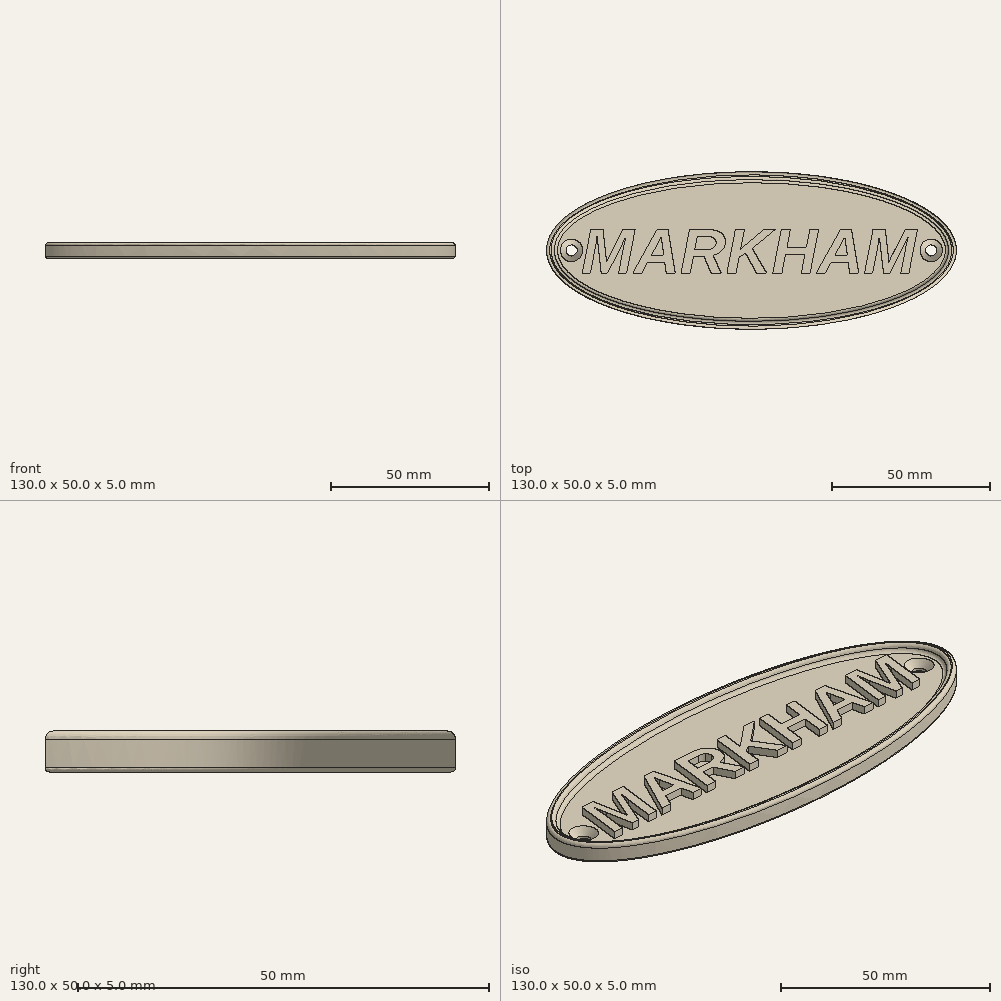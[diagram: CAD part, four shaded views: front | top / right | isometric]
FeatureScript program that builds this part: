
annotation { "Feature Type Name" : "Feature", "Feature Type Description" : "" }
export const myFeature = defineFeature(function(context is Context, id is Id, definition is map)
    precondition{}
    {
        {
            var Q0;
            Q0=qCreatedBy(makeId("Top.planeOp"),FACE);
            var sketch = newSketch(context, id + "F0", { "sketchPlane" : qUnion([Q0])});
            skEllipse(sketch, "E0", {"center": v(0, 0) * mm, "majorRadius": 65 * mm, "minorRadius": 25 * mm, "majorAxis": v(1, 0)});
            skSolve(sketch);
        }
        {
            var Q0;
            Q0=makeQuery(id+"F0.imprint","IMPRINT",FACE,{"disambiguationData":[TD([[makeQuery(id+"F0.imprint","IMPRINT",EDGE,{"derivedFrom":sQuery(id+"F0.wireOp",EDGE,"E0")}),1.0]])]});
            extrude(context, id + "F1", {"entities" : qUnion([Q0]), "depth" : 3 * mm, "offsetDistance" : 25 * mm});
        }
        {
            var Q0;
            Q0=makeQuery(id+"F1.opExtrude","CAP_FACE",FACE,{"disambiguationData":[OSD([sQuery(id+"F0.wireOp",EDGE,"E0")])],"isStart":false});
            var sketch = newSketch(context, id + "F2", { "sketchPlane" : qUnion([Q0])});
            skEllipse(sketch, "E1", {"center": v(0, 0) * mm, "majorRadius": 65 * mm, "minorRadius": 25 * mm, "majorAxis": v(1, 0)});
            skEllipse(sketch, "E2", {"center": v(0, 0) * mm, "majorRadius": 62.5 * mm, "minorRadius": 22.5 * mm, "majorAxis": v(1, 0)});
            skText(sketch, "E3", { "text": "MARKHAM", "fontName": "Arimo-BoldItalic.ttf"});
            const initialGuessF2  = {"E3": [-0.054, -0.00725, 1, 0, 0.0145]};
            skSetInitialGuess(sketch, initialGuessF2);
            skSolve(sketch);
        }
        {
            var Q0;
            Q0=makeQuery(id+"F2.imprint","IMPRINT",FACE,{"disambiguationData":[TD([[makeQuery(id+"F2.imprint","IMPRINT",EDGE,{"derivedFrom":sQuery(id+"F2.wireOp",EDGE,"E1")}),1.0]])]});
            var Q1;
            Q1=makeQuery(id+"F2.imprint","IMPRINT",FACE,{"disambiguationData":[TD([[makeQuery(id+"F2.imprint","IMPRINT",EDGE,{"derivedFrom":sQuery(id+"F2.wireOp",EDGE,"E3.sketch_text.stroke-0")}),-1.0]])]});
            var Q2;
            Q2=makeQuery(id+"F2.imprint","IMPRINT",FACE,{"disambiguationData":[TD([[makeQuery(id+"F2.imprint","IMPRINT",EDGE,{"derivedFrom":sQuery(id+"F2.wireOp",EDGE,"E3.sketch_text.stroke-20")}),-1.0]])]});
            var Q3;
            Q3=makeQuery(id+"F2.imprint","IMPRINT",FACE,{"disambiguationData":[TD([[makeQuery(id+"F2.imprint","IMPRINT",EDGE,{"derivedFrom":sQuery(id+"F2.wireOp",EDGE,"E3.sketch_text.stroke-33")}),-1.0]])]});
            var Q4;
            Q4=makeQuery(id+"F2.imprint","IMPRINT",FACE,{"disambiguationData":[TD([[makeQuery(id+"F2.imprint","IMPRINT",EDGE,{"derivedFrom":sQuery(id+"F2.wireOp",EDGE,"E3.sketch_text.stroke-53")}),-1.0]])]});
            var Q5;
            Q5=makeQuery(id+"F2.imprint","IMPRINT",FACE,{"disambiguationData":[TD([[makeQuery(id+"F2.imprint","IMPRINT",EDGE,{"derivedFrom":sQuery(id+"F2.wireOp",EDGE,"E3.sketch_text.stroke-65")}),-1.0]])]});
            var Q6;
            Q6=makeQuery(id+"F2.imprint","IMPRINT",FACE,{"disambiguationData":[TD([[makeQuery(id+"F2.imprint","IMPRINT",EDGE,{"derivedFrom":sQuery(id+"F2.wireOp",EDGE,"E3.sketch_text.stroke-77")}),-1.0]])]});
            var Q7;
            Q7=makeQuery(id+"F2.imprint","IMPRINT",FACE,{"disambiguationData":[TD([[makeQuery(id+"F2.imprint","IMPRINT",EDGE,{"derivedFrom":sQuery(id+"F2.wireOp",EDGE,"E3.sketch_text.stroke-90")}),-1.0]])]});
            extrude(context, id + "F3", {"entities" : qUnion([Q0, Q1, Q2, Q3, Q4, Q5, Q6, Q7]), "operationType" : NewBodyOperationType.ADD, "depth" : 2 * mm, "offsetDistance" : 25 * mm});
        }
        {
            var Q0;
            Q0=qCreatedBy(makeId("Top.planeOp"),FACE);
            var sketch = newSketch(context, id + "F4", { "sketchPlane" : qUnion([Q0])});
            skLineSegment(sketch, "E4", {"start": v(0, 0) * mm, "end": v(-57, 0) * mm, "construction": true});
            skLineSegment(sketch, "E5", {"start": v(0, 0) * mm, "end": v(57, 0) * mm, "construction": true});
            skCircle(sketch, "E6", {"center": v(-57, 0) * mm, "radius": 1.75 * mm});
            skCircle(sketch, "E7", {"center": v(57, 0) * mm, "radius": 1.75 * mm});
            skSolve(sketch);
        }
        {
            var Q0;
            Q0 = qSketchRegion(id + "F4", true);
            extrude(context, id + "F5", {"entities" : qUnion([Q0]), "operationType" : NewBodyOperationType.REMOVE, "oppositeDirection" : true, "depth" : 1 * mm, "offsetDistance" : 25 * mm, "hasSecondDirection" : true, "secondDirectionOppositeDirection" : false, "secondDirectionDepth" : 4 * mm});
        }
        {
            var Q0;
            Q0=makeQuery(id+"F5.boolean.opBoolean","INTERSECT",EDGE,{"derivedFrom":[makeQuery(id+"F3.boolean.opBoolean","SPLIT",FACE,{"disambiguationData":[TD([makeQuery(id+"F3.opExtrude","SWEPT_FACE",FACE,{"disambiguationData":[OSD([sQuery(id+"F2.wireOp",EDGE,"E2")])]})])],"derivedFrom":makeQuery(id+"F1.opExtrude","CAP_FACE",FACE,{"disambiguationData":[OSD([sQuery(id+"F0.wireOp",EDGE,"E0")])],"isStart":false})}),makeQuery(id+"F5.opExtrude","SWEPT_FACE",FACE,{"disambiguationData":[OSD([sQuery(id+"F4.wireOp",EDGE,"E6")])]})]});
            var Q1;
            Q1=makeQuery(id+"F5.boolean.opBoolean","INTERSECT",EDGE,{"derivedFrom":[makeQuery(id+"F3.boolean.opBoolean","SPLIT",FACE,{"disambiguationData":[TD([makeQuery(id+"F3.opExtrude","SWEPT_FACE",FACE,{"disambiguationData":[OSD([sQuery(id+"F2.wireOp",EDGE,"E2")])]})])],"derivedFrom":makeQuery(id+"F1.opExtrude","CAP_FACE",FACE,{"disambiguationData":[OSD([sQuery(id+"F0.wireOp",EDGE,"E0")])],"isStart":false})}),makeQuery(id+"F5.opExtrude","SWEPT_FACE",FACE,{"disambiguationData":[OSD([sQuery(id+"F4.wireOp",EDGE,"E7")])]})]});
            chamfer(context, id + "F6", {"entities" : qUnion([Q0, Q1]), "width" : 1.8 * mm, "tangentPropagation" : true});
        }
        {
            var Q0;
            Q0=makeQuery(id+"F3.opExtrude","CAP_FACE",FACE,{"disambiguationData":[OSD([sQuery(id+"F2.wireOp",EDGE,"E1"),sQuery(id+"F2.wireOp",EDGE,"E2")])],"isStart":false});
            fillet(context, id + "F7", {"entities" : qUnion([Q0]), "radius" : 1 * mm, "tangentPropagation" : true, "allowEdgeOverflow" : false});
        }
        {
            var Q0;
            Q0=makeQuery(id+"F3.opExtrude","CAP_EDGE",EDGE,{"disambiguationData":[OSD([sQuery(id+"F2.wireOp",EDGE,"E2")])],"isStart":true});
            fillet(context, id + "F8", {"entities" : qUnion([Q0]), "radius" : 1 * mm, "tangentPropagation" : true, "allowEdgeOverflow" : false});
        }
        {
            var Q0;
            Q0=makeQuery(id+"F1.opExtrude","CAP_FACE",FACE,{"disambiguationData":[OSD([sQuery(id+"F0.wireOp",EDGE,"E0")])],"isStart":true});
            fillet(context, id + "F9", {"entities" : qUnion([Q0]), "radius" : .5 * mm, "tangentPropagation" : true, "allowEdgeOverflow" : false});
        }
    });
